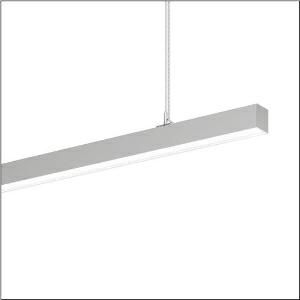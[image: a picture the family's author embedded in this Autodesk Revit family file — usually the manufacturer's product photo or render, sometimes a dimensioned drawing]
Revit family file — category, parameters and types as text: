
# Revit family: silica_r__21_51mx30tbt5s_71cb
name_source: partatom
category: Lighting Fixtures
units: mm (PartAtom-declared; Revit-internal decimal feet)

## family parameters
Cut with Voids When Loaded = No
Host = Face
Light Source = No
Part Type = Normal
Room Calculation Point = No
Round Connector Dimension = Use Diameter
Shared = No

## types (1)
- --- (1 x LED, 5150 lm, 42.2 W, 6500K)
    Apparent Load = 42 VA
    CIE Flux Codes = 47 79 96 58 100
    Color Rendering = 80
    Color Temperature = 6500K
    Default Elevation = 1800 mm
    Description = Silica® 21, office luminaire, primary optical cover: cover, of PMMA, opal, light emission: direct/indirect distribution, primary light characteristic: symmetric, installation type: suspended mounting, LED, rated luminous flux: 5.150lm, luminous efficacy: 116lm/W, light colour: 8tw, colour temperature: 2700..6500K, control gear: ECG DALI, with terminal, 3+2-pole, max. 2.5mm², mains connection: 220..240V, AC, 50/60Hz, rated input power: 44.3W, luminaire housing, of aluminium, metallic grey (RAL 9006), length: 1.504mm, width: 53mm, height: 53mm, protection rating (complete): IP20, insulation class (complete): insulation class I (protective earthing), certification: CE, permissible operating ambient temperature: 0..+35°C, standard: EN 50419, packaging unit: 1 piece
    Height = 53 mm
    Lamp = 1 x LED
    Lamp Light Flux = 5150 lm
    Lamp Power = 42.2 W
    Lamp count = 1
    Length = 1504 mm
    Luminous efficacy = 122 lm/W
    Manufacturer = Siteco
    ModVariant = No
    Model = 51MX30TBT5S
    Mounting Place = Ceiling
    Mounting Type = Pendant
    Number of Poles = 1
    OnlyDefault = Yes
    Power Factor = 1
    Product Name = Silica® 21
    Product group = office luminaire | ceiling pendant
    ProductGroupID = 902
    Protection Class = Protection class I
    Protection Degree = IP 20
    RLX_Detail_Level = 1
    RLX_Emergency_Light_Flux = 0 lm
    RLX_Emergency_Type = 0
    RLX_Emergency_Type_DB = No
    RlxData = <blob elided: 20189 chars, md5=34dce681>
    Socket = socket
    Standby Power = 0 W
    System Light Flux = 5150 lm
    System Power = 42 W
    Type Comments = individual setting
    Type Image = l_1297747.jpg
    URL = http://relux.com
    VarID = @adj_070939
    Voltage = 0 V
    Weight = 0.00 kg
    Width = 53 mm

## geometry (parser evidence)
native form markers: Blend x4, Sweep x12
no freeform markers — native parametric forms only
